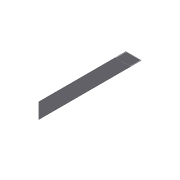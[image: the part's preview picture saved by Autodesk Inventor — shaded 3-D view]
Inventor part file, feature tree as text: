
AUTODESK INVENTOR PART (.ipt)
format: ipt  version: 2012 (Build 160160000, 160)  size: 72,192 bytes
history: native  units: in
note: dims shown in document units (in); Inventor stores cm internally (conversion verified against a paired STEP export)
features: extrude x1, shell x1, sketch x1
ambient origin geometry x8: Origin, YZ Plane, XZ Plane, XY Plane, X Axis, Y Axis, Z Axis, Center Point
bodies: Solid1 (feature_tree)
feature tree (3):
  extrude  "Extrusion1"  Depth=7.0in
  shell  "Shell1"  Thickness=7.0in
  sketch  "Sketch1"  dims[d0=1.0in d2=7.0in d3=7.0in d4=1.0in d5=0.0in d6=0.0625in]
